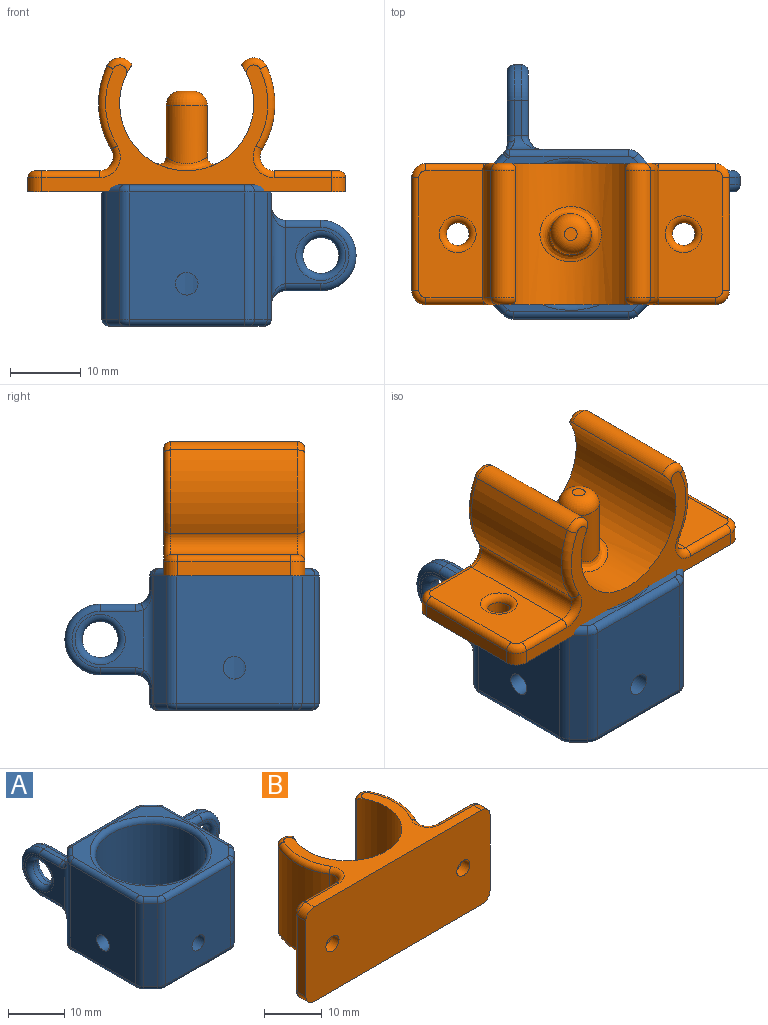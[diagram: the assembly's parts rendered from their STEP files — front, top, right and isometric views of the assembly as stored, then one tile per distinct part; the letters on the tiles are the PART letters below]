
ASSEMBLY  parts=2 mates=1
PART A: 109 faces, bbox 36.9x36.9x20 mm
  f0: plane 18x16.79mm, normal (1,0,0), area 237.6mm2, adj f25,f26,f27,f37,f45,f46,f72,f73
  f1: plane 18x16.79mm, normal (0,1,0), area 237.6mm2, adj f29,f30,f31,f38,f60,f67,f88,f92
  f2: plane 18x1.83mm, normal (-0.71,0.71,0), area 46.5mm2, adj f32,f33,f56,f86
  f3: plane 18x16.34mm, normal (-1,0,0), area 286.1mm2, adj f20,f33,f34,f50,f80
  f4: plane 18x1.83mm, normal (-0.71,-0.71,0), area 46.5mm2, adj f34,f35,f44,f74
  f5: plane 18x16.34mm, normal (0,-1,0), area 286.1mm2, adj f19,f35,f36,f40,f66
  f6: plane 18x1.83mm, normal (0.71,-0.71,0), area 46.5mm2, adj f36,f37,f41,f65
  f7: cylinder r=9.8mm len=19.6mm, axis (0,0,-1), area 1092.2mm2, adj f19,f20,f107,f108
  f8: plane 18x1.83mm, normal (0.71,0.71,0), area 46.5mm2, adj f28,f38,f54,f82
  f9: plane 22x22mm, normal (0,0,1), area 105.8mm2, adj f62,f65,f66,f69,f70,f73,f74,f77
  f10: plane 22x22mm, normal (0,0,-1), area 105.8mm2, adj f39,f40,f41,f42,f43,f44,f45,f47
  f11: plane 9x8mm, normal (1,0,0), area 25.5mm2, adj f29,f94,f95,f96,f103
  f12: plane 10.17x8.48mm, normal (-1,0,0), area 35.1mm2, adj f32,f75,f78,f81,f84,f87,f104
  f13: plane 5x1mm, normal (0,0,1), area 5mm2, adj f24,f30,f84,f96
  f14: plane 5x1mm, normal (0,0,-1), area 5mm2, adj f24,f31,f78,f94
  f15: plane 10.17x8.48mm, normal (0,1,0), area 35.1mm2, adj f28,f52,f55,f58,f61,f64,f106
  f16: plane 9x8mm, normal (0,-1,0), area 25.5mm2, adj f25,f99,f100,f101,f105
  f17: plane 5x1mm, normal (0,0,1), area 5mm2, adj f23,f26,f61,f101
  f18: plane 5x1mm, normal (0,0,-1), area 5mm2, adj f23,f27,f55,f99
  f19: cylinder r=1.6mm len=3.2mm, axis (0,-1,0), area 22.8mm2, adj f5,f7
  f20: cylinder r=1.6mm len=3.2mm, axis (-1,0,0), area 22.8mm2, adj f3,f7
  f21: cylinder r=2.55mm len=5.1mm, axis (0,1,0), area 16mm2, adj f105,f106
  f22: cylinder r=2.55mm len=5.1mm, axis (-1,0,0), area 16mm2, adj f103,f104
  f23: cylinder r=5mm len=10mm, axis (0,-1,0), area 15.7mm2, adj f17,f18,f58,f100
  f24: cylinder r=5mm len=10mm, axis (1,0,0), area 15.7mm2, adj f13,f14,f81,f95
  f25: cylinder r=2mm len=14mm, axis (0,0,1), area 32mm2, adj f0,f16,f98,f102
  f26: cylinder r=2mm len=4.62mm, axis (0,1,0), area 7.3mm2, adj f0,f17,f64,f68,f102
  f27: cylinder r=2mm len=4.62mm, axis (0,-1,0), area 7.3mm2, adj f0,f18,f49,f52,f98
  f28: cylinder r=2mm len=18mm, axis (0,0,-1), area 17.9mm2, adj f8,f15,f46,f49,f51,f68,f72,f79
  f29: cylinder r=2mm len=14mm, axis (0,0,1), area 32mm2, adj f1,f11,f93,f97
  f30: cylinder r=2mm len=4.62mm, axis (-1,0,0), area 7.3mm2, adj f1,f13,f87,f90,f97
  f31: cylinder r=2mm len=4.62mm, axis (1,0,0), area 7.3mm2, adj f1,f14,f71,f75,f93
  f32: cylinder r=2mm len=18mm, axis (0,0,-1), area 17.9mm2, adj f2,f12,f59,f67,f71,f89,f90,f92
  f33: cylinder r=2mm len=18mm, axis (0,0,1), area 28.3mm2, adj f2,f3,f53,f83
  f34: cylinder r=2mm len=18mm, axis (0,0,-1), area 28.3mm2, adj f3,f4,f47,f77
  f35: cylinder r=2mm len=18mm, axis (0,0,-1), area 28.3mm2, adj f4,f5,f42,f70
  f36: cylinder r=2mm len=18mm, axis (0,0,1), area 28.3mm2, adj f5,f6,f39,f62
  f37: cylinder r=2mm len=18mm, axis (0,0,-1), area 28.3mm2, adj f0,f6,f43,f69
  f38: cylinder r=2mm len=18mm, axis (0,0,-1), area 28.3mm2, adj f1,f8,f57,f85
  f39: torus R=1mm, axis (0,0,1), area 2mm2, adj f10,f36,f40,f41
  f40: cylinder r=1mm len=16.34mm, axis (1,0,0), area 25.7mm2, adj f5,f10,f39,f42
  f41: cylinder r=1mm len=2.54mm, axis (0.71,0.71,0), area 4.1mm2, adj f6,f10,f39,f43
  f42: torus R=1mm, axis (0,0,1), area 2mm2, adj f10,f35,f40,f44
  f43: torus R=1mm, axis (0,0,1), area 2mm2, adj f10,f37,f41,f45
  f44: cylinder r=1mm len=2.54mm, axis (0.71,-0.71,0), area 4.1mm2, adj f4,f10,f42,f47
  f45: cylinder r=1mm len=16.79mm, axis (0,1,0), area 26.4mm2, adj f0,f10,f43,f48
  f46: cylinder r=1mm len=2mm, axis (0,0,-1), area 1.8mm2, adj f0,f28,f48,f49
  f47: torus R=1mm, axis (0,0,1), area 2mm2, adj f10,f34,f44,f50
  f48: sphere r=1mm, area 0.9mm2, adj f45,f46,f51
  f49: bspline ~3.53x1.93mm, area 3.2mm2, adj f27,f28,f46,f52
  f50: cylinder r=1mm len=16.34mm, axis (0,-1,0), area 25.7mm2, adj f3,f10,f47,f53
  f51: torus R=3mm, axis (0,0,1), area 0.5mm2, adj f10,f28,f48,f54
  f52: torus R=3mm, axis (0,1,0), area 1.5mm2, adj f15,f27,f49,f55
  f53: torus R=1mm, axis (0,0,1), area 2mm2, adj f10,f33,f50,f56
  f54: cylinder r=1mm len=2.54mm, axis (-0.71,0.71,0), area 4.1mm2, adj f8,f10,f51,f57
  f55: cylinder r=1mm len=5mm, axis (-1,0,0), area 7.9mm2, adj f15,f18,f52,f58
  f56: cylinder r=1mm len=2.54mm, axis (-0.71,-0.71,0), area 4.1mm2, adj f2,f10,f53,f59
  f57: torus R=1mm, axis (0,0,1), area 2mm2, adj f10,f38,f54,f60
  f58: torus R=4mm, axis (0,1,0), area 22.9mm2, adj f15,f23,f55,f61
  f59: torus R=3mm, axis (0,0,1), area 0.5mm2, adj f10,f32,f56,f63
  f60: cylinder r=1mm len=16.79mm, axis (-1,0,0), area 26.4mm2, adj f1,f10,f57,f63
  f61: cylinder r=1mm len=5mm, axis (1,0,0), area 7.9mm2, adj f15,f17,f58,f64
  f62: torus R=1mm, axis (0,0,1), area 2mm2, adj f9,f36,f65,f66
  f63: sphere r=1mm, area 0.9mm2, adj f59,f60,f67
  f64: torus R=3mm, axis (0,1,0), area 1.5mm2, adj f15,f26,f61,f68
  f65: cylinder r=1mm len=2.54mm, axis (-0.71,-0.71,0), area 4.1mm2, adj f6,f9,f62,f69
  f66: cylinder r=1mm len=16.34mm, axis (-1,0,0), area 25.7mm2, adj f5,f9,f62,f70
  f67: cylinder r=1mm len=2mm, axis (0,0,-1), area 1.8mm2, adj f1,f32,f63,f71
  f68: bspline ~3.53x1.93mm, area 3.2mm2, adj f26,f28,f64,f72
  f69: torus R=1mm, axis (0,0,1), area 2mm2, adj f9,f37,f65,f73
  f70: torus R=1mm, axis (0,0,1), area 2mm2, adj f9,f35,f66,f74
  f71: bspline ~3.53x1.93mm, area 3.2mm2, adj f31,f32,f67,f75
  f72: cylinder r=1mm len=2mm, axis (0,0,-1), area 1.8mm2, adj f0,f28,f68,f76
  f73: cylinder r=1mm len=16.79mm, axis (0,-1,0), area 26.4mm2, adj f0,f9,f69,f76
  f74: cylinder r=1mm len=2.54mm, axis (-0.71,0.71,0), area 4.1mm2, adj f4,f9,f70,f77
  f75: torus R=3mm, axis (-1,0,0), area 1.5mm2, adj f12,f31,f71,f78
  f76: sphere r=1mm, area 0.9mm2, adj f72,f73,f79
  f77: torus R=1mm, axis (0,0,1), area 2mm2, adj f9,f34,f74,f80
  f78: cylinder r=1mm len=5mm, axis (0,-1,0), area 7.9mm2, adj f12,f14,f75,f81
  f79: torus R=3mm, axis (0,0,1), area 0.5mm2, adj f9,f28,f76,f82
  f80: cylinder r=1mm len=16.34mm, axis (0,1,0), area 25.7mm2, adj f3,f9,f77,f83
  f81: torus R=4mm, axis (-1,0,0), area 22.9mm2, adj f12,f24,f78,f84
  f82: cylinder r=1mm len=2.54mm, axis (0.71,-0.71,0), area 4.1mm2, adj f8,f9,f79,f85
  f83: torus R=1mm, axis (0,0,1), area 2mm2, adj f9,f33,f80,f86
  f84: cylinder r=1mm len=5mm, axis (0,1,0), area 7.9mm2, adj f12,f13,f81,f87
  f85: torus R=1mm, axis (0,0,1), area 2mm2, adj f9,f38,f82,f88
  f86: cylinder r=1mm len=2.54mm, axis (0.71,0.71,0), area 4.1mm2, adj f2,f9,f83,f89
  f87: torus R=3mm, axis (-1,0,0), area 1.5mm2, adj f12,f30,f84,f90
  f88: cylinder r=1mm len=16.79mm, axis (1,0,0), area 26.4mm2, adj f1,f9,f85,f91
  f89: torus R=3mm, axis (0,0,1), area 0.5mm2, adj f9,f32,f86,f91
  f90: bspline ~3.53x1.93mm, area 3.2mm2, adj f30,f32,f87,f92
  f91: sphere r=1mm, area 0.9mm2, adj f88,f89,f92
  f92: cylinder r=1mm len=2mm, axis (0,0,-1), area 1.8mm2, adj f1,f32,f90,f91
  f93: bspline ~3x3mm, area 3.6mm2, adj f29,f31,f94
  f94: cylinder r=1mm len=5mm, axis (0,1,0), area 7.9mm2, adj f11,f14,f93,f95
  f95: torus R=4mm, axis (-1,0,0), area 22.9mm2, adj f11,f24,f94,f96
  f96: cylinder r=1mm len=5mm, axis (0,-1,0), area 7.9mm2, adj f11,f13,f95,f97
  f97: bspline ~3x3mm, area 3.6mm2, adj f29,f30,f96
  f98: bspline ~3x3mm, area 3.6mm2, adj f25,f27,f99
  f99: cylinder r=1mm len=5mm, axis (1,0,0), area 7.9mm2, adj f16,f18,f98,f100
  f100: torus R=4mm, axis (0,1,0), area 22.9mm2, adj f16,f23,f99,f101
  f101: cylinder r=1mm len=5mm, axis (-1,0,0), area 7.9mm2, adj f16,f17,f100,f102
  f102: bspline ~3x3mm, area 3.6mm2, adj f25,f26,f101
  f103: torus R=3.55mm, axis (-1,0,0), area 28.8mm2, adj f11,f22
  f104: torus R=3.55mm, axis (-1,0,0), area 28.8mm2, adj f12,f22
  f105: torus R=3.55mm, axis (0,1,0), area 28.8mm2, adj f16,f21
  f106: torus R=3.55mm, axis (0,1,0), area 28.8mm2, adj f15,f21
  f107: torus R=10.8mm, axis (0,0,1), area 100.3mm2, adj f7,f10
  f108: torus R=10.8mm, axis (0,0,1), area 100.3mm2, adj f7,f9
PART B: 48 faces, bbox 45.3x19.2x20.3 mm
  f0: cylinder r=9.5mm len=20mm, axis (0,0,-1), area 775.5mm2, adj f8,f9,f16,f17,f23,f33,f34,f44
  f1: plane 45x20mm, normal (0,-1,0), area 880.5mm2, adj f2,f7,f8,f9,f10,f11,f19,f20
  f2: plane 16x2mm, normal (1,0,0), area 32mm2, adj f1,f19,f21,f39
  f3: plane 18x9.09mm, normal (0,1,0), area 142mm2, adj f15,f37,f38,f39,f40,f41,f46
  f4: cylinder r=12.5mm len=18mm, axis (0,0,-1), area 222mm2, adj f15,f16,f35,f43
  f5: cylinder r=12.5mm len=18mm, axis (0,0,-1), area 222mm2, adj f17,f18,f24,f32
  f6: plane 18x9.09mm, normal (0,1,0), area 142mm2, adj f18,f26,f27,f28,f29,f30,f47
  f7: plane 16x2mm, normal (-1,0,0), area 32mm2, adj f1,f20,f22,f28
  f8: plane 41x18mm, normal (0,0,1), area 182.4mm2, adj f0,f1,f21,f22,f30,f31,f32,f33
  f9: plane 41x18mm, normal (0,0,-1), area 182.4mm2, adj f0,f1,f19,f20,f23,f24,f25,f26
  f10: cylinder r=1.6mm len=3.2mm, axis (0,1,0), area 20.1mm2, adj f1,f47
  f11: cylinder r=1.6mm len=3.2mm, axis (0,1,0), area 20.1mm2, adj f1,f46
  f12: cylinder r=2.9mm len=8.3mm, axis (0,-1,0), area 142.7mm2, adj f14,f45
  f13: plane 1.8x1.8mm, normal (0,1,0), area 2.5mm2, adj f14
  f14: torus R=0.9mm, axis (0,1,0), area 42.9mm2, adj f12,f13
  f15: cylinder r=2mm len=18mm, axis (0,0,-1), area 76.1mm2, adj f3,f4,f36,f42
  f16: cylinder r=2mm len=18mm, axis (0,0,1), area 78.4mm2, adj f0,f4,f34,f44
  f17: cylinder r=2mm len=18mm, axis (0,0,1), area 78.4mm2, adj f0,f5,f23,f33
  f18: cylinder r=2mm len=18mm, axis (0,0,-1), area 76.1mm2, adj f5,f6,f25,f31
  f19: cylinder r=2mm len=2mm, axis (0,1,0), area 6.3mm2, adj f1,f2,f9,f38
  f20: cylinder r=2mm len=2mm, axis (0,-1,0), area 6.3mm2, adj f1,f7,f9,f27
  f21: cylinder r=2mm len=2mm, axis (0,-1,0), area 6.3mm2, adj f1,f2,f8,f40
  f22: cylinder r=2mm len=2mm, axis (0,1,0), area 6.3mm2, adj f1,f7,f8,f29
  f23: torus R=1mm, axis (0,0,1), area 5.9mm2, adj f0,f9,f17,f24
  f24: torus R=11.5mm, axis (0,0,1), area 18.8mm2, adj f5,f9,f23,f25
  f25: torus R=3mm, axis (0,0,1), area 7.8mm2, adj f9,f18,f24,f26
  f26: cylinder r=1mm len=8.09mm, axis (-1,0,0), area 12.7mm2, adj f6,f9,f25,f27
  f27: torus R=1mm, axis (0,-1,0), area 4mm2, adj f6,f20,f26,f28
  f28: cylinder r=1mm len=16mm, axis (0,0,-1), area 25.1mm2, adj f6,f7,f27,f29
  f29: torus R=1mm, axis (0,-1,0), area 4mm2, adj f6,f22,f28,f30
  f30: cylinder r=1mm len=8.09mm, axis (1,0,0), area 12.7mm2, adj f6,f8,f29,f31
  f31: torus R=3mm, axis (0,0,1), area 7.8mm2, adj f8,f18,f30,f32
  f32: torus R=11.5mm, axis (0,0,1), area 18.8mm2, adj f5,f8,f31,f33
  f33: torus R=1mm, axis (0,0,1), area 5.9mm2, adj f0,f8,f17,f32
  f34: torus R=1mm, axis (0,0,1), area 5.9mm2, adj f0,f9,f16,f35
  f35: torus R=11.5mm, axis (0,0,1), area 18.8mm2, adj f4,f9,f34,f36
  f36: torus R=3mm, axis (0,0,1), area 7.8mm2, adj f9,f15,f35,f37
  f37: cylinder r=1mm len=8.09mm, axis (-1,0,0), area 12.7mm2, adj f3,f9,f36,f38
  f38: torus R=1mm, axis (0,-1,0), area 4mm2, adj f3,f19,f37,f39
  f39: cylinder r=1mm len=16mm, axis (0,0,1), area 25.1mm2, adj f2,f3,f38,f40
  f40: torus R=1mm, axis (0,-1,0), area 4mm2, adj f3,f21,f39,f41
  f41: cylinder r=1mm len=8.09mm, axis (1,0,0), area 12.7mm2, adj f3,f8,f40,f42
  f42: torus R=3mm, axis (0,0,1), area 7.8mm2, adj f8,f15,f41,f43
  f43: torus R=11.5mm, axis (0,0,1), area 18.8mm2, adj f4,f8,f42,f44
  f44: torus R=1mm, axis (0,0,1), area 5.9mm2, adj f0,f8,f16,f43
  f45: bspline ~8.73x7.81mm, area 38.6mm2, adj f0,f12
  f46: torus R=2.6mm, axis (0,-1,0), area 19.4mm2, adj f3,f11
  f47: torus R=2.6mm, axis (0,-1,0), area 19.4mm2, adj f6,f10
PLACE A at identity
PLACE B rot(axis=(1,0,0),90deg) t=(0,0,9)mm
MATE fastened B.f12 <-> A.f7  axis (0,0,-1) through (0,0,9)mm
